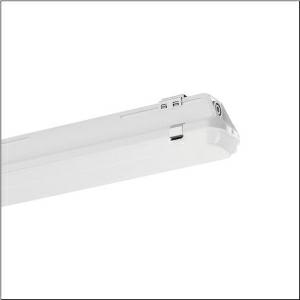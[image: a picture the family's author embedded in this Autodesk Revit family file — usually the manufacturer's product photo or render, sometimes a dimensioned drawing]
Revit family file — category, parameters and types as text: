
# Revit family: monsun_r__11_51fp12mp4b0u_05f5
name_source: partatom
category: Lighting Fixtures
units: mm (PartAtom-declared; Revit-internal decimal feet)

## family parameters
Cut with Voids When Loaded = No
Host = Face
Light Source = No
Part Type = Normal
Room Calculation Point = No
Round Connector Dimension = Use Diameter
Shared = No

## types (1)
- --- (1 x LED, 11850 lm, 62.4 W, 4000K)
    Apparent Load = 62 VA
    CIE Flux Codes = 62 86 96 97 100
    Color Rendering = 80
    Color Temperature = 4000K
    Default Elevation = 1800 mm
    Description = Monsun® 11, damp-proof luminaire, chain hanger, primary light control with lens, primary optical cover: enclosure, of PMMA, light emission: direct distribution, primary light characteristic: symmetric, installation type: suspended mounting, surface-mounted, horizontal mounting, vertical mounting, LED, rated luminous flux: 11.850lm, luminous efficacy: 190lm/W, light colour: 840, colour temperature: 4000K, control gear: ON/OFF Multilumen, with terminal, 3-pole, max. 2.5mm², mains connection: 220..240V, AC, 50/60Hz, rated input power: 62W, luminaire housing, of glass-fibre reinforced polyester, uncoated, bright grey, incl. chain hanger, length: 1.590mm, width: 90mm, height: 88mm, clip for enclosure, of stainless steel (V2A), ceiling mounting element, of stainless steel (V2A), chain hanger, of stainless steel (V2A), protection rating (complete): IP66, insulation class (complete): insulation class I (protective earthing), certification: CE, ENEC, VDE, UKCA, protection symbol: D, impact resistance: IK04, permissible operating ambient temperature: -35..+35°C, standard: EN 50419, EN 60598-2-1, contact your sales advisor before using the luminaires in applications with unclear chemical exposure, large temperature fluctuations or condensation-forming humidity, LABS conformity tested according to VDMA 24364:2018-05, no direct snow, no direct sun, no direct rain, for indoor or canopied outdoor use, corresponds to IFS (International Featured Standards) requirements for safety and quality in the food industry, packaging unit: 1 piece
    Height = 89 mm
    Lamp = 1 x LED
    Lamp Light Flux = 11850 lm
    Lamp Power = 62.4 W
    Lamp count = 1
    Length = 1590 mm
    Luminous efficacy = 190 lm/W
    Manufacturer = Siteco
    ModVariant = No
    Model = 51FP12MP4B0U
    Mounting Place = Ceiling
    Mounting Type = Surface mounted
    Number of Poles = 1
    OnlyDefault = Yes
    Power Factor = 1
    Product Name = Monsun® 11
    Product group = damp-proof luminaire
    ProductGroupID = 300
    Protection Class = Protection class I
    Protection Degree = IP 66
    RLX_Detail_Level = 1
    RLX_Emergency_Light_Flux = 0 lm
    RLX_Emergency_Type = 0
    RLX_Emergency_Type_DB = No
    RlxData = <blob elided: 89913 chars, md5=1df2109e>
    Socket = socket
    Standby Power = 0 W
    System Light Flux = 11850 lm
    System Power = 62 W
    Type Comments = factory setting: luminous flux: 100 % | (A | C | E) | 147 mA
    Type Image = l_1349237.jpg
    URL = http://relux.com
    VarID = @adj_018660
    Voltage = 0 V
    Weight = 0.00 kg
    Width = 90 mm

## geometry (parser evidence)
native form markers: Blend x4, Sweep x9
no freeform markers — native parametric forms only
